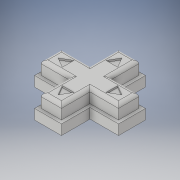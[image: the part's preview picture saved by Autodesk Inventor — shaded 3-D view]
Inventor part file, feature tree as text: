
AUTODESK INVENTOR PART (.ipt)
format: ipt  version: 2019 (Build 230136000, 136)  size: 193,024 bytes
history: native  units: mm
features: extrude x3, sketch x3, fillet x1
ambient origin geometry x8: Origin, YZ Plane, XZ Plane, XY Plane, X Axis, Y Axis, Z Axis, Center Point
bodies: Volumenkörper1 (feature_tree)
feature tree (7):
  extrude  "Extrusion1"  Depth=23.0mm
  extrude  "Extrusion2"  Depth=6.0mm
  fillet  "Rundung1"  Radius=8.5mm
  extrude  "Extrusion3"  Depth=8.5mm
  sketch  "Skizze1"  dims[d0=23.0mm d1=23.0mm]
  sketch  "Skizze2"  dims[d2=6.0mm d3=6.0mm d4=8.5mm]
  sketch  "Skizze3"  dims[d5=8.5mm d6=8.5mm d7=4.0mm d8=0.0mm d9=4.0mm d10=3.0mm d11=4.0mm d12=4.0mm d13=4.0mm d14=3.0mm d15=3.0mm d16=3.0mm d17=3.5mm d18=3.5mm d19=3.5mm d20=3.5mm d21=0.5mm d22=0.0mm d23=1.0mm d25=8.5mm d26=25.0mm d27=25.0mm d28=8.0mm d29=8.0mm d30=8.0mm d31=8.0mm d32=8.5mm d33=8.5mm d34=8.5mm d35=8.5mm d36=8.5mm d37=3.0mm d38=0.0mm]
